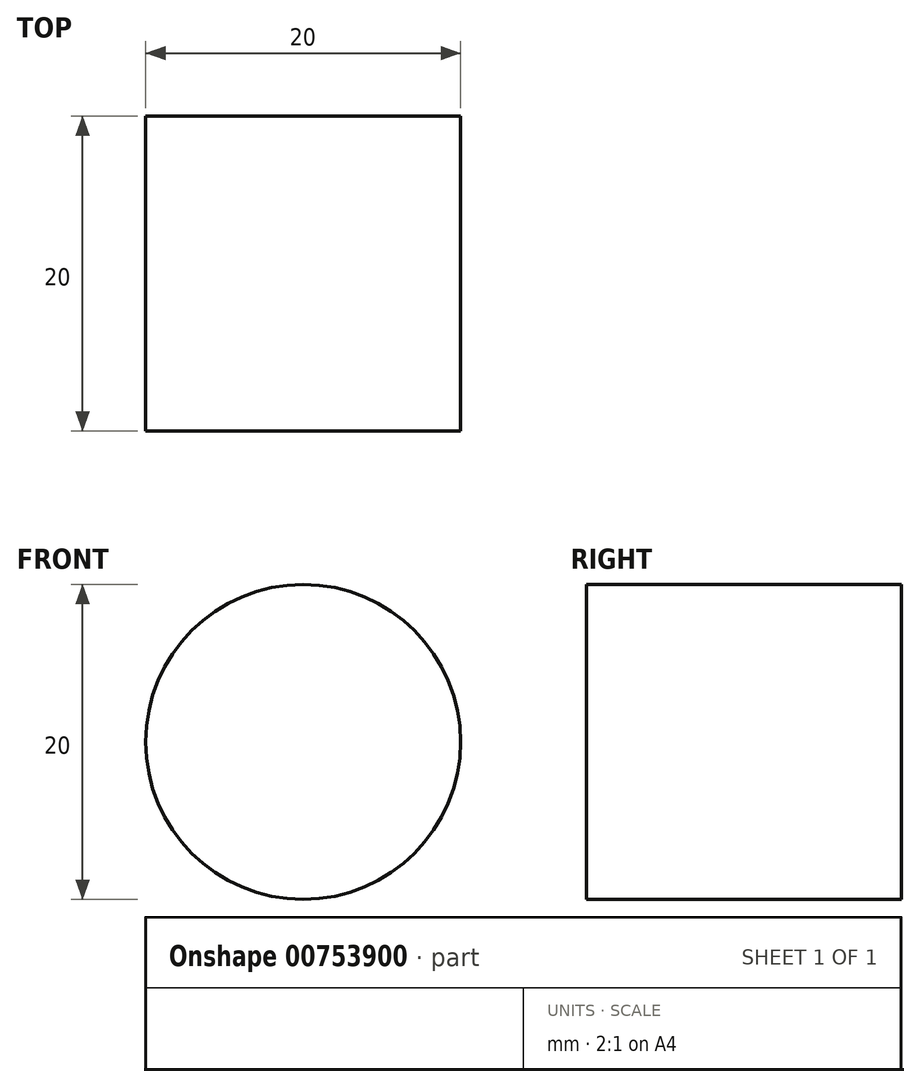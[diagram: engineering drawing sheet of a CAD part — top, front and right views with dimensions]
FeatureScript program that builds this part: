
annotation { "Feature Type Name" : "Feature", "Feature Type Description" : "" }
export const myFeature = defineFeature(function(context is Context, id is Id, definition is map)
    precondition{}
    {
        {
            var Q0;
            Q0=qCreatedBy(makeId("Front.planeOp"),FACE);
            var sketch = newSketch(context, id + "F0", { "sketchPlane" : qUnion([Q0])});
            skCircle(sketch, "E0", {"center": v(0, 0) * mm, "radius": 10 * mm});
            skSolve(sketch);
        }
        {
            var Q0;
            Q0 = qSketchRegion(id + "F0", true);
            extrude(context, id + "F1", {"entities" : qUnion([Q0]), "depth" : 20 * mm, "offsetDistance" : 25 * mm});
        }
    });
